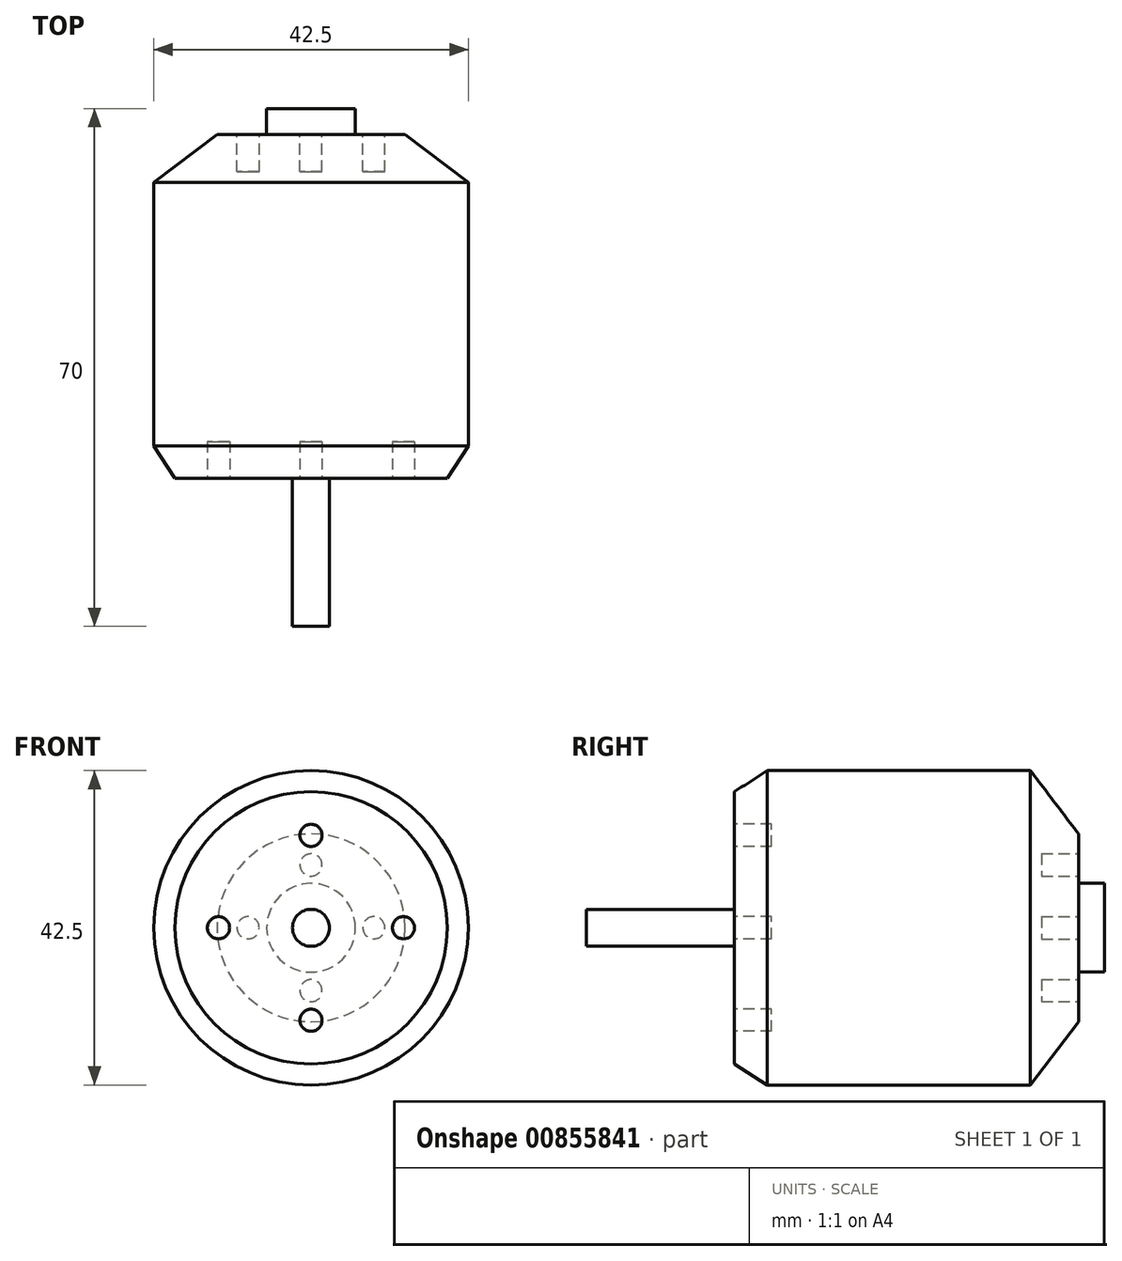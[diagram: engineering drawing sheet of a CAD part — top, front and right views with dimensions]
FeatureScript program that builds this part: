
annotation { "Feature Type Name" : "Feature", "Feature Type Description" : "" }
export const myFeature = defineFeature(function(context is Context, id is Id, definition is map)
    precondition{}
    {
        {
            var Q0;
            Q0=qCreatedBy(makeId("Right.planeOp"),FACE);
            var sketch = newSketch(context, id + "F0", { "sketchPlane" : qUnion([Q0])});
            skLineSegment(sketch, "E0", {"start": v(-20, 0) * mm, "end": v(-20, 2.5) * mm});
            skLineSegment(sketch, "E1", {"start": v(-20, 2.5) * mm, "end": v(0, 2.5) * mm});
            skLineSegment(sketch, "E2", {"start": v(0, 2.5) * mm, "end": v(0, 18.4) * mm});
            skLineSegment(sketch, "E3", {"start": v(0, 18.4) * mm, "end": v(4.4, 21.25) * mm});
            skLineSegment(sketch, "E4", {"start": v(4.4, 21.25) * mm, "end": v(40, 21.25) * mm});
            skLineSegment(sketch, "E5", {"start": v(40, 21.25) * mm, "end": v(46.5, 12.7) * mm});
            skLineSegment(sketch, "E6", {"start": v(46.5, 12.7) * mm, "end": v(46.5, 6) * mm});
            skLineSegment(sketch, "E7", {"start": v(46.5, 6) * mm, "end": v(50, 6) * mm});
            skLineSegment(sketch, "E8", {"start": v(50, 6) * mm, "end": v(50, 0) * mm});
            skLineSegment(sketch, "E9", {"start": v(50, 0) * mm, "end": v(-20, 0) * mm});
            skSolve(sketch);
        }
        {
            var Q0;
            Q0=makeQuery(id+"F0.imprint","IMPRINT",FACE,{"disambiguationData":[TD([[makeQuery(id+"F0.imprint","IMPRINT",EDGE,{"derivedFrom":sQuery(id+"F0.wireOp",EDGE,"E0")}),-1.0]])]});
            var Q1;
            Q1=sQuery(id+"F0.wireOp",EDGE,"E9");
            revolve(context, id + "F1", {"surfaceOperationType" : NewSurfaceOperationType.NEW, "entities" : qUnion([Q0]), "axis" : qUnion([Q1]), "revolveType" : RevolveType.FULL});
        }
        {
            var Q0;
            Q0=makeQuery(id+"F1.opRevolve","SWEPT_FACE",FACE,{"disambiguationData":[OSD([sQuery(id+"F0.wireOp",EDGE,"E2")])]});
            var sketch = newSketch(context, id + "F2", { "sketchPlane" : qUnion([Q0])});
            skCircle(sketch, "E10", {"center": v(12.5, 0) * mm, "radius": 1.5 * mm});
            skCircle(sketch, "E11.1.0", {"center": v(0, 12.5) * mm, "radius": 1.5 * mm});
            skCircle(sketch, "E11.2.0", {"center": v(-12.5, 0) * mm, "radius": 1.5 * mm});
            skCircle(sketch, "E11.3.0", {"center": v(0, -12.5) * mm, "radius": 1.5 * mm});
            skPoint(sketch, "E11.center", {"position": v(0, 0) * mm});
            skSolve(sketch);
        }
        {
            var Q0;
            Q0=qSketchRegion(id+"F2",true);
            extrude(context, id + "F3", {"entities" : qUnion([Q0]), "operationType" : NewBodyOperationType.REMOVE, "oppositeDirection" : true, "depth" : 5 * mm, "offsetDistance" : 25 * mm});
        }
        {
            var Q0;
            Q0=makeQuery(id+"F1.opRevolve","SWEPT_FACE",FACE,{"disambiguationData":[OSD([sQuery(id+"F0.wireOp",EDGE,"E6")])]});
            var sketch = newSketch(context, id + "F4", { "sketchPlane" : qUnion([Q0])});
            skCircle(sketch, "E12", {"center": v(8.5, 0) * mm, "radius": 1.5 * mm});
            skCircle(sketch, "E13.1.0", {"center": v(0, 8.5) * mm, "radius": 1.5 * mm});
            skCircle(sketch, "E13.2.0", {"center": v(-8.5, 0) * mm, "radius": 1.5 * mm});
            skCircle(sketch, "E13.3.0", {"center": v(0, -8.5) * mm, "radius": 1.5 * mm});
            skPoint(sketch, "E13.center", {"position": v(0, 0) * mm});
            skSolve(sketch);
        }
        {
            var Q0;
            Q0=qSketchRegion(id+"F4",true);
            extrude(context, id + "F5", {"entities" : qUnion([Q0]), "operationType" : NewBodyOperationType.REMOVE, "oppositeDirection" : true, "depth" : 5 * mm, "offsetDistance" : 25 * mm});
        }
    });
